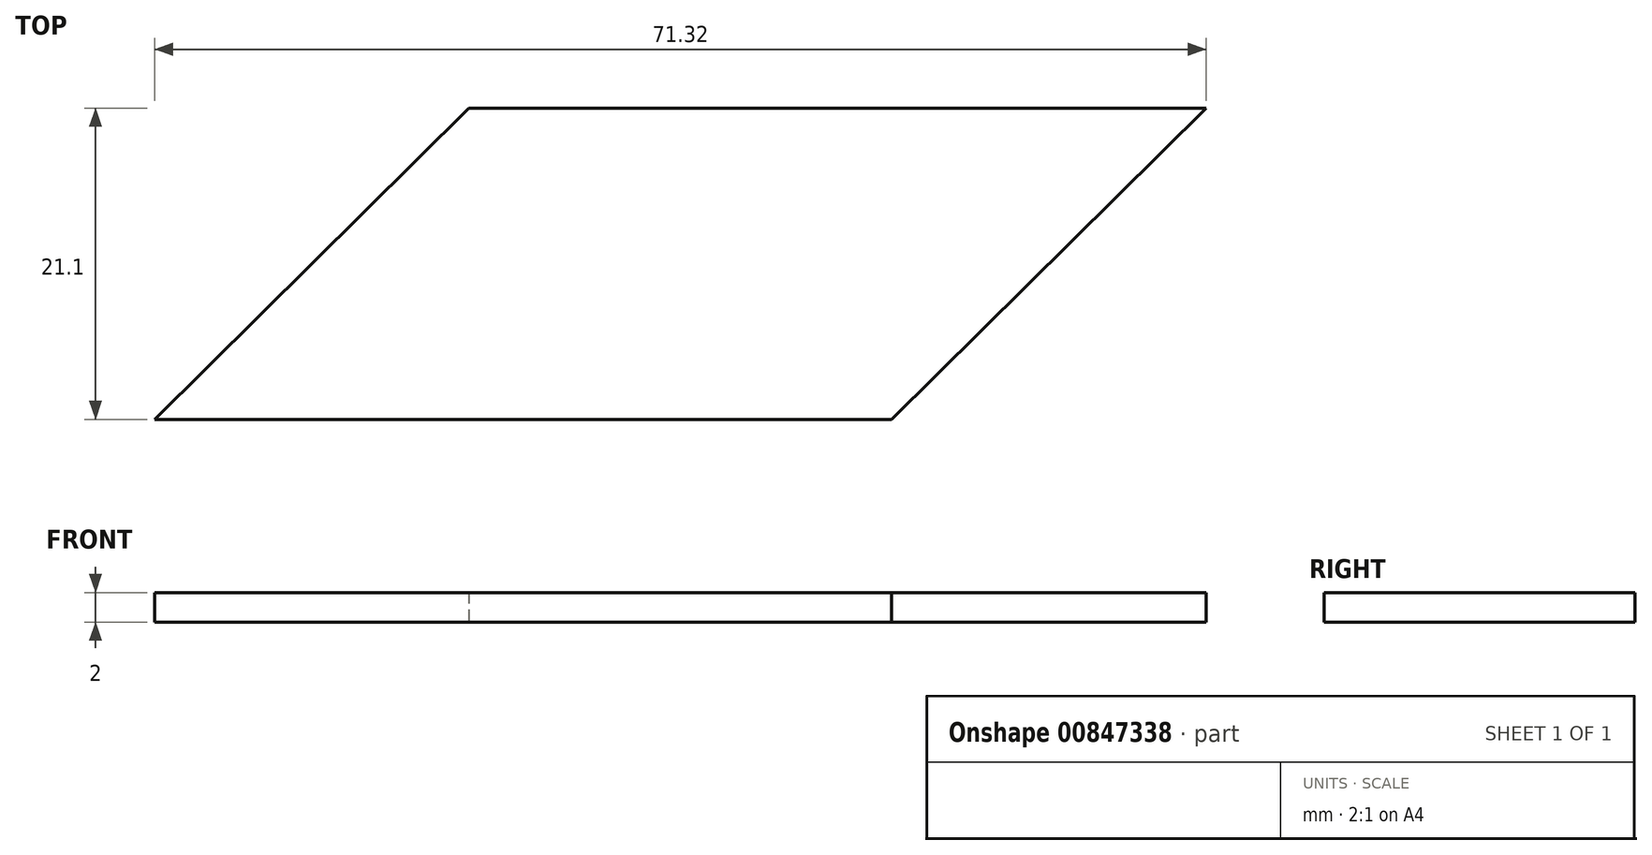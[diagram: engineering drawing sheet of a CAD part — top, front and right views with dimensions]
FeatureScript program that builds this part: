
annotation { "Feature Type Name" : "Feature", "Feature Type Description" : "" }
export const myFeature = defineFeature(function(context is Context, id is Id, definition is map)
    precondition{}
    {
        {
            var Q0;
            Q0=qCreatedBy(makeId("Top.planeOp"),FACE);
            var sketch = newSketch(context, id + "F0", { "sketchPlane" : qUnion([Q0])});
            skLineSegment(sketch, "E0", {"start": v(-50, 0) * mm, "end": v(0, 0) * mm});
            skLineSegment(sketch, "E1", {"start": v(-50, 0) * mm, "end": v(-28.68, 21.1) * mm});
            skLineSegment(sketch, "E2", {"start": v(-28.68, 21.1) * mm, "end": v(21.32, 21.1) * mm});
            skLineSegment(sketch, "E3", {"start": v(21.32, 21.1) * mm, "end": v(0, 0) * mm});
            skSolve(sketch);
        }
        {
            var Q0;
            Q0 = qSketchRegion(id + "F0", true);
            extrude(context, id + "F1", {"entities" : qUnion([Q0]), "depth" : 2 * mm, "offsetDistance" : 25 * mm});
        }
    });
